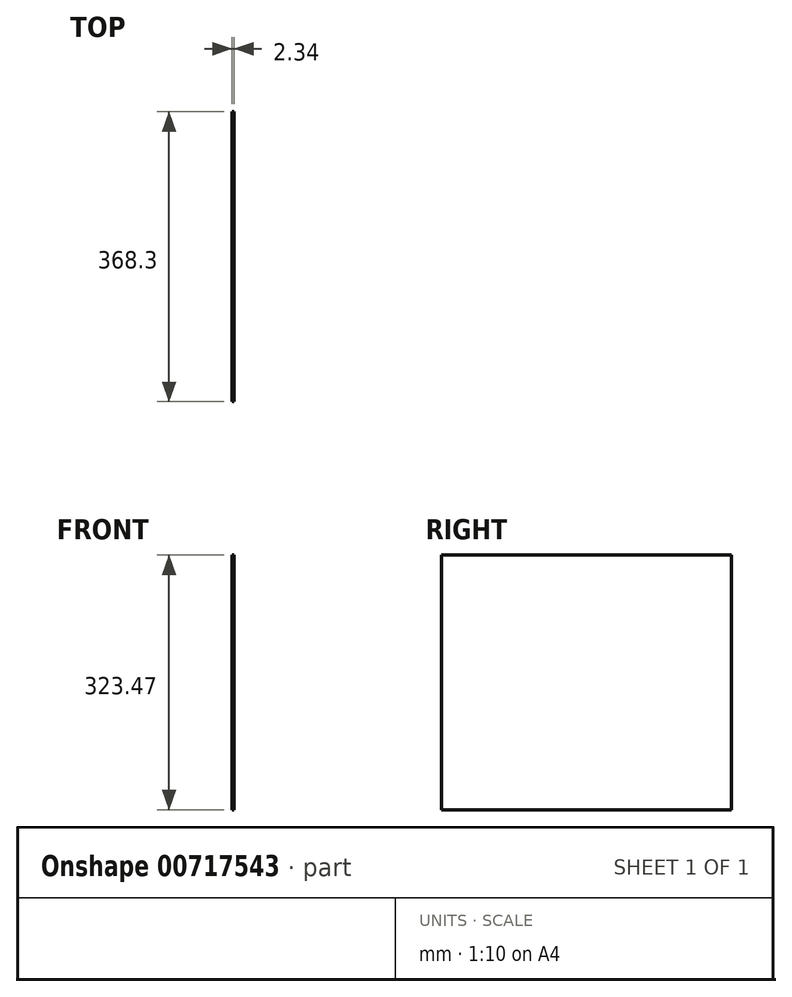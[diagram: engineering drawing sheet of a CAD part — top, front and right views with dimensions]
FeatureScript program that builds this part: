
annotation { "Feature Type Name" : "Feature", "Feature Type Description" : "" }
export const myFeature = defineFeature(function(context is Context, id is Id, definition is map)
    precondition{}
    {
        {
            var Q0;
            Q0=qCreatedBy(makeId("Front.planeOp"),FACE);
            var sketch = newSketch(context, id + "F0", { "sketchPlane" : qUnion([Q0])});
            skLineSegment(sketch, "E0.bottom", {"start": v(-66.65, 249.19) * mm, "end": v(-64.31, 249.19) * mm});
            skLineSegment(sketch, "E0.top", {"start": v(-66.65, -74.28) * mm, "end": v(-64.31, -74.28) * mm});
            skLineSegment(sketch, "E0.left", {"start": v(-64.31, 249.19) * mm, "end": v(-64.31, -74.28) * mm});
            skLineSegment(sketch, "E0.right", {"start": v(-66.65, 249.19) * mm, "end": v(-66.65, -74.28) * mm});
            skSolve(sketch);
        }
        {
            var Q0;
            Q0=makeQuery(id+"F0.imprint","IMPRINT",FACE,{"disambiguationData":[TD([[makeQuery(id+"F0.imprint","IMPRINT",EDGE,{"derivedFrom":sQuery(id+"F0.wireOp",EDGE,"E0.bottom")}),-1.0]])]});
            extrude(context, id + "F1", {"entities" : qUnion([Q0]), "depth" : 368.3 * mm, "offsetDistance" : 25.4 * mm});
        }
    });
